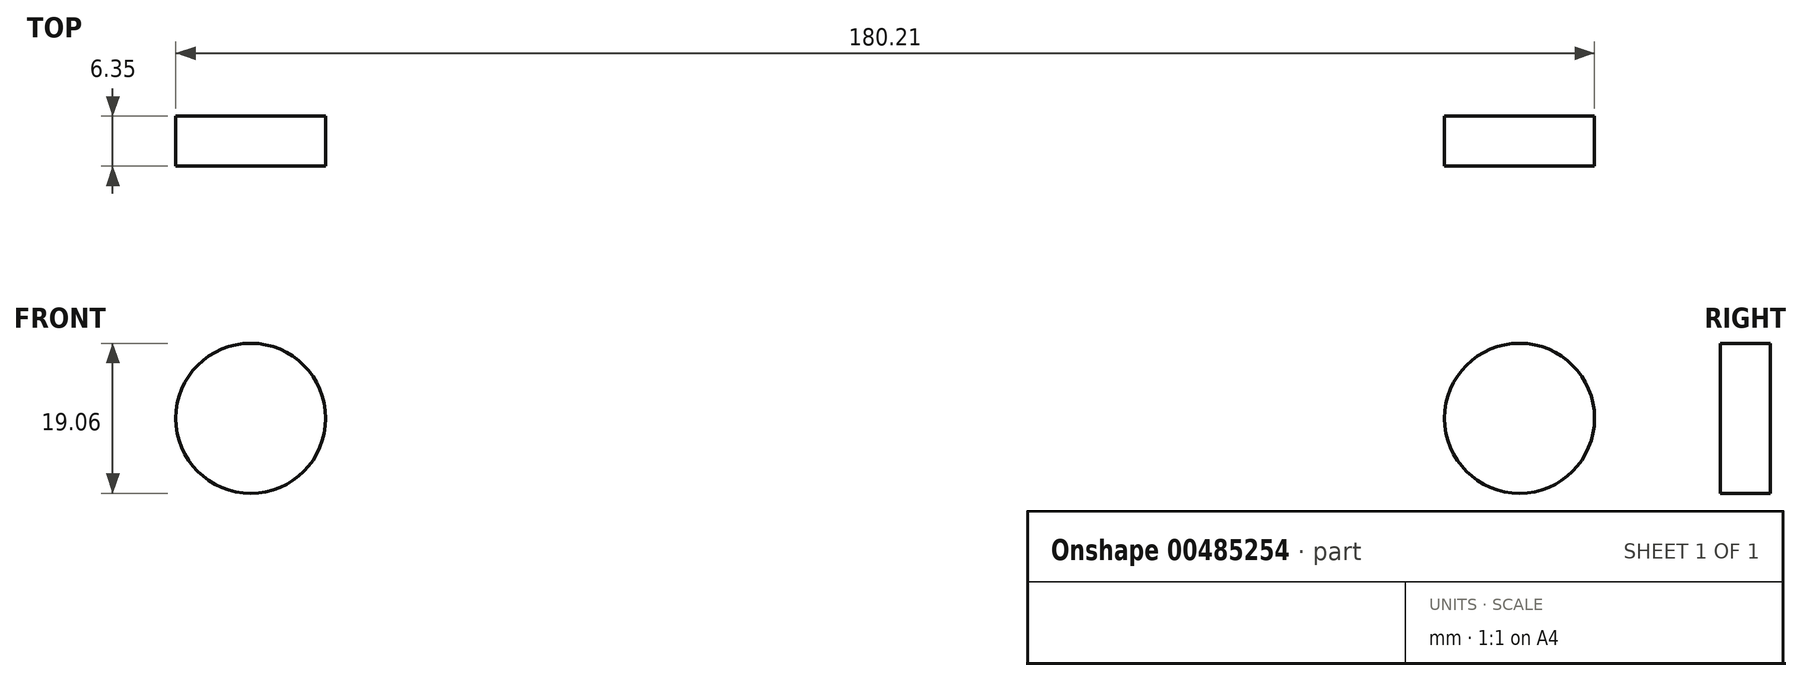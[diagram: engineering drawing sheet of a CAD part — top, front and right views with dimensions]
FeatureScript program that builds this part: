
annotation { "Feature Type Name" : "Feature", "Feature Type Description" : "" }
export const myFeature = defineFeature(function(context is Context, id is Id, definition is map)
    precondition{}
    {
        {
            var Q0;
            Q0=qCreatedBy(makeId("Front.planeOp"),FACE);
            var sketch = newSketch(context, id + "F0", { "sketchPlane" : qUnion([Q0])});
            skLineSegment(sketch, "E0.bottom", {"start": v(127, -25.4) * mm, "end": v(-127, -25.4) * mm});
            skLineSegment(sketch, "E0.top", {"start": v(127, 25.4) * mm, "end": v(-127, 25.4) * mm});
            skLineSegment(sketch, "E0.left", {"start": v(127, -25.4) * mm, "end": v(127, 25.4) * mm});
            skLineSegment(sketch, "E0.right", {"start": v(-127, -25.4) * mm, "end": v(-127, 25.4) * mm});
            skPoint(sketch, "E0.middle", {"position": v(0, 0) * mm});
            skCircle(sketch, "E1", {"center": v(81.76, 0) * mm, "radius": 9.52 * mm});
            skCircle(sketch, "E2", {"center": v(-79.4, 0) * mm, "radius": 9.52 * mm});
            skSolve(sketch);
        }
        {
            var Q0;
            Q0=makeQuery(id+"F0.imprint","IMPRINT",FACE,{"disambiguationData":[TD([[makeQuery(id+"F0.imprint","IMPRINT",EDGE,{"derivedFrom":sQuery(id+"F0.wireOp",EDGE,"E2")}),1.0]])]});
            var Q1;
            Q1=makeQuery(id+"F0.imprint","IMPRINT",FACE,{"disambiguationData":[TD([[makeQuery(id+"F0.imprint","IMPRINT",EDGE,{"derivedFrom":sQuery(id+"F0.wireOp",EDGE,"E1")}),1.0]])]});
            extrude(context, id + "F1", {"entities" : qUnion([Q0, Q1]), "depth" : 6.35 * mm});
        }
    });
